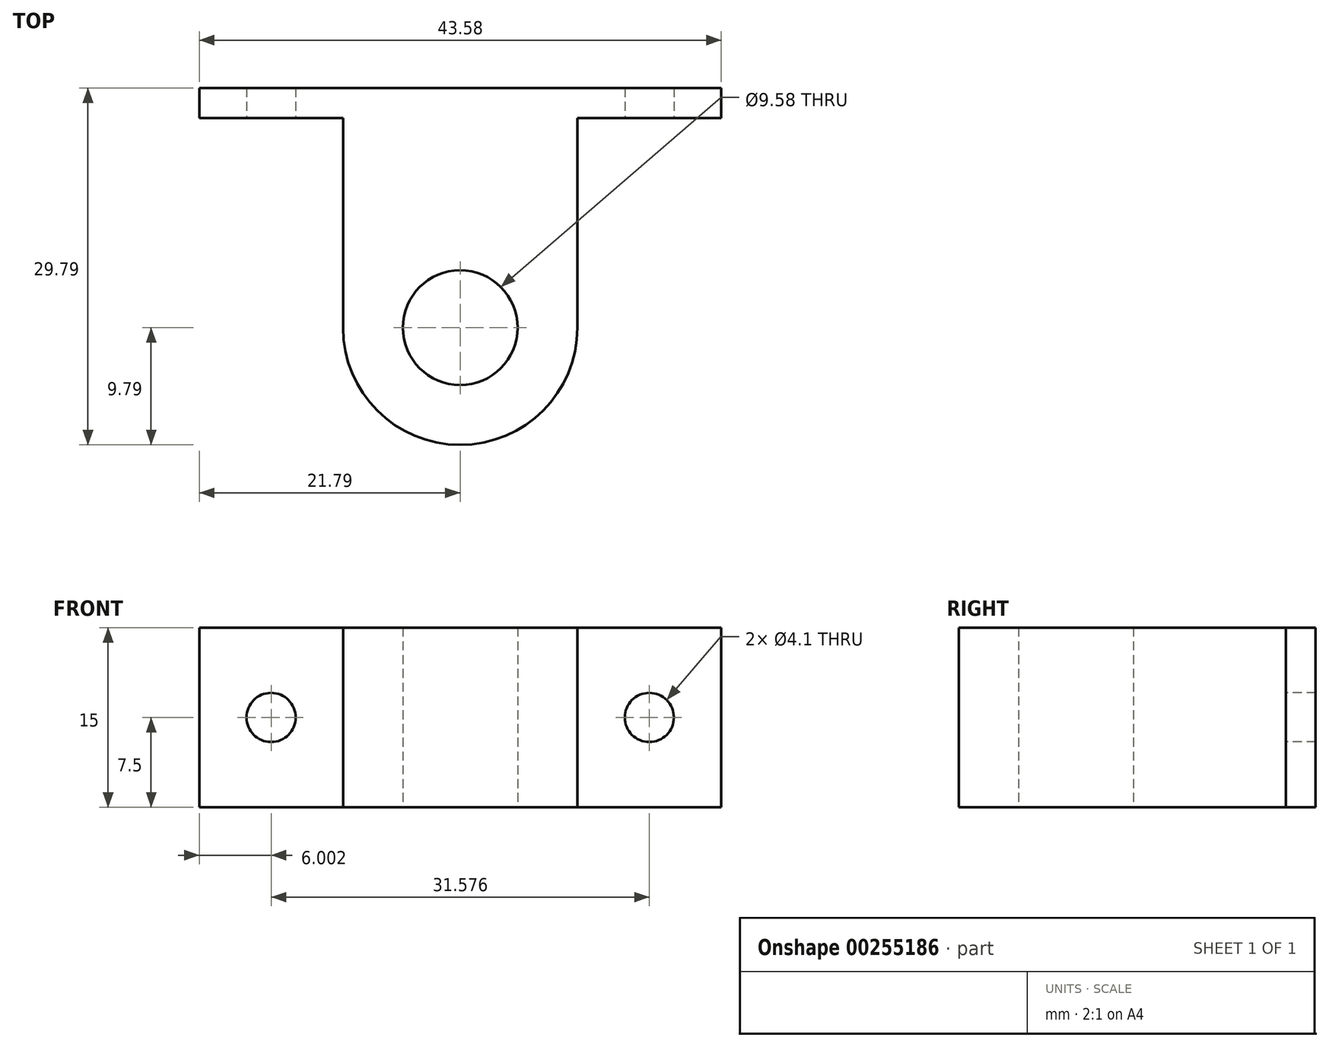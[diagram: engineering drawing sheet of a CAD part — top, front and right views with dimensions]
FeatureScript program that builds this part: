
annotation { "Feature Type Name" : "Feature", "Feature Type Description" : "" }
export const myFeature = defineFeature(function(context is Context, id is Id, definition is map)
    precondition{}
    {
        {
            var Q0;
            Q0=qCreatedBy(makeId("Top.planeOp"),FACE);
            var sketch = newSketch(context, id + "F0", { "sketchPlane" : qUnion([Q0])});
            skCircle(sketch, "E0", {"center": v(0, 0) * mm, "radius": 4.79 * mm});
            skCircle(sketch, "E1.0", {"center": v(0, 0) * mm, "radius": 9.79 * mm});
            skLineSegment(sketch, "E2", {"start": v(-9.79, 0) * mm, "end": v(-9.79, 17.5) * mm});
            skLineSegment(sketch, "E3", {"start": v(-9.79, 17.5) * mm, "end": v(-21.79, 17.5) * mm});
            skLineSegment(sketch, "E4", {"start": v(-21.79, 17.5) * mm, "end": v(-21.79, 20) * mm});
            skLineSegment(sketch, "E5", {"start": v(-21.79, 20) * mm, "end": v(0, 20) * mm});
            skLineSegment(sketch, "E6", {"start": v(0, 20) * mm, "end": v(0, 0) * mm, "construction": true});
            skLineSegment(sketch, "E7.MirrorCS", {"start": v(21.79, 20) * mm, "end": v(0, 20) * mm});
            skLineSegment(sketch, "E8.MirrorCS", {"start": v(9.79, 0) * mm, "end": v(9.79, 17.5) * mm});
            skLineSegment(sketch, "E9.MirrorCS", {"start": v(9.79, 17.5) * mm, "end": v(21.79, 17.5) * mm});
            skLineSegment(sketch, "E10.MirrorCS", {"start": v(21.79, 17.5) * mm, "end": v(21.79, 20) * mm});
            skSolve(sketch);
        }
        {
            var Q0;
            {var subQ0=sQuery(id+"F0.wireOp",EDGE,"E2");Q0=makeQuery(id+"F0.imprint","IMPRINT",FACE,{"disambiguationData":[TD([[makeQuery(id+"F0.imprint","IMPRINT",EDGE,{"derivedFrom":subQ0}),-1.0]])]});}
            var Q1;
            Q1=makeQuery(id+"F0.imprint","IMPRINT",FACE,{"disambiguationData":[TD([[makeQuery(id+"F0.imprint","IMPRINT",EDGE,{"derivedFrom":sQuery(id+"F0.wireOp",EDGE,"E0")}),-1.0]])]});
            extrude(context, id + "F1", {"entities" : qUnion([Q0, Q1]), "depth" : 15 * mm});
        }
        {
            var Q0;
            Q0=makeQuery(id+"F1.opExtrude","SWEPT_FACE",FACE,{"disambiguationData":[OSD([sQuery(id+"F0.wireOp",EDGE,"E3")])]});
            var sketch = newSketch(context, id + "F2", { "sketchPlane" : qUnion([Q0])});
            skLineSegment(sketch, "E11", {"start": v(-21.79, 7.5) * mm, "end": v(-9.79, 7.5) * mm, "construction": true});
            skPoint(sketch, "E12", {"position": v(-15.79, 7.5) * mm});
            skSolve(sketch);
        }
        {
            var Q0;
            Q0=makeQuery(id+"F1.opExtrude","SWEPT_FACE",FACE,{"disambiguationData":[OSD([sQuery(id+"F0.wireOp",EDGE,"E9.MirrorCS")])]});
            var sketch = newSketch(context, id + "F3", { "sketchPlane" : qUnion([Q0])});
            skLineSegment(sketch, "E13", {"start": v(21.79, 7.5) * mm, "end": v(9.79, 7.5) * mm, "construction": true});
            skPoint(sketch, "E14", {"position": v(15.79, 7.5) * mm});
            skSolve(sketch);
        }
        {
            var Q0;
            Q0=sQuery(id+"F3.wireOp",VERTEX,"E14");
            var Q1;
            Q1=makeQuery(id+"F1.opExtrude","SWEPT_BODY",BODY,{"disambiguationData":[OSD([sQuery(id+"F0.wireOp",EDGE,"E0"),sQuery(id+"F0.wireOp",EDGE,"E1.0"),sQuery(id+"F0.wireOp",EDGE,"E2"),sQuery(id+"F0.wireOp",EDGE,"E3"),sQuery(id+"F0.wireOp",EDGE,"E4"),sQuery(id+"F0.wireOp",EDGE,"E5"),sQuery(id+"F0.wireOp",EDGE,"E7.MirrorCS"),sQuery(id+"F0.wireOp",EDGE,"E8.MirrorCS"),sQuery(id+"F0.wireOp",EDGE,"E9.MirrorCS"),sQuery(id+"F0.wireOp",EDGE,"E10.MirrorCS")])]});
            hole(context, id + "F4", {"style" : HoleStyle.SIMPLE, "endStyle" : HoleEndStyle.THROUGH, "holeDiameter" : 4.1 * mm, "tappedDepth" : 12 * mm, "tapClearance" : 3, "locations" : qUnion([Q0]), "scope" : qUnion([Q1])});
        }
        {
            var Q0;
            Q0=sQuery(id+"F2.wireOp",VERTEX,"E12");
            var Q1;
            Q1=makeQuery(id+"F1.opExtrude","SWEPT_BODY",BODY,{"disambiguationData":[OSD([sQuery(id+"F0.wireOp",EDGE,"E0"),sQuery(id+"F0.wireOp",EDGE,"E1.0"),sQuery(id+"F0.wireOp",EDGE,"E2"),sQuery(id+"F0.wireOp",EDGE,"E3"),sQuery(id+"F0.wireOp",EDGE,"E4"),sQuery(id+"F0.wireOp",EDGE,"E5"),sQuery(id+"F0.wireOp",EDGE,"E7.MirrorCS"),sQuery(id+"F0.wireOp",EDGE,"E8.MirrorCS"),sQuery(id+"F0.wireOp",EDGE,"E9.MirrorCS"),sQuery(id+"F0.wireOp",EDGE,"E10.MirrorCS")])]});
            hole(context, id + "F5", {"style" : HoleStyle.SIMPLE, "endStyle" : HoleEndStyle.THROUGH, "holeDiameter" : 4.1 * mm, "tappedDepth" : 12 * mm, "tapClearance" : 3, "locations" : qUnion([Q0]), "scope" : qUnion([Q1])});
        }
    });
